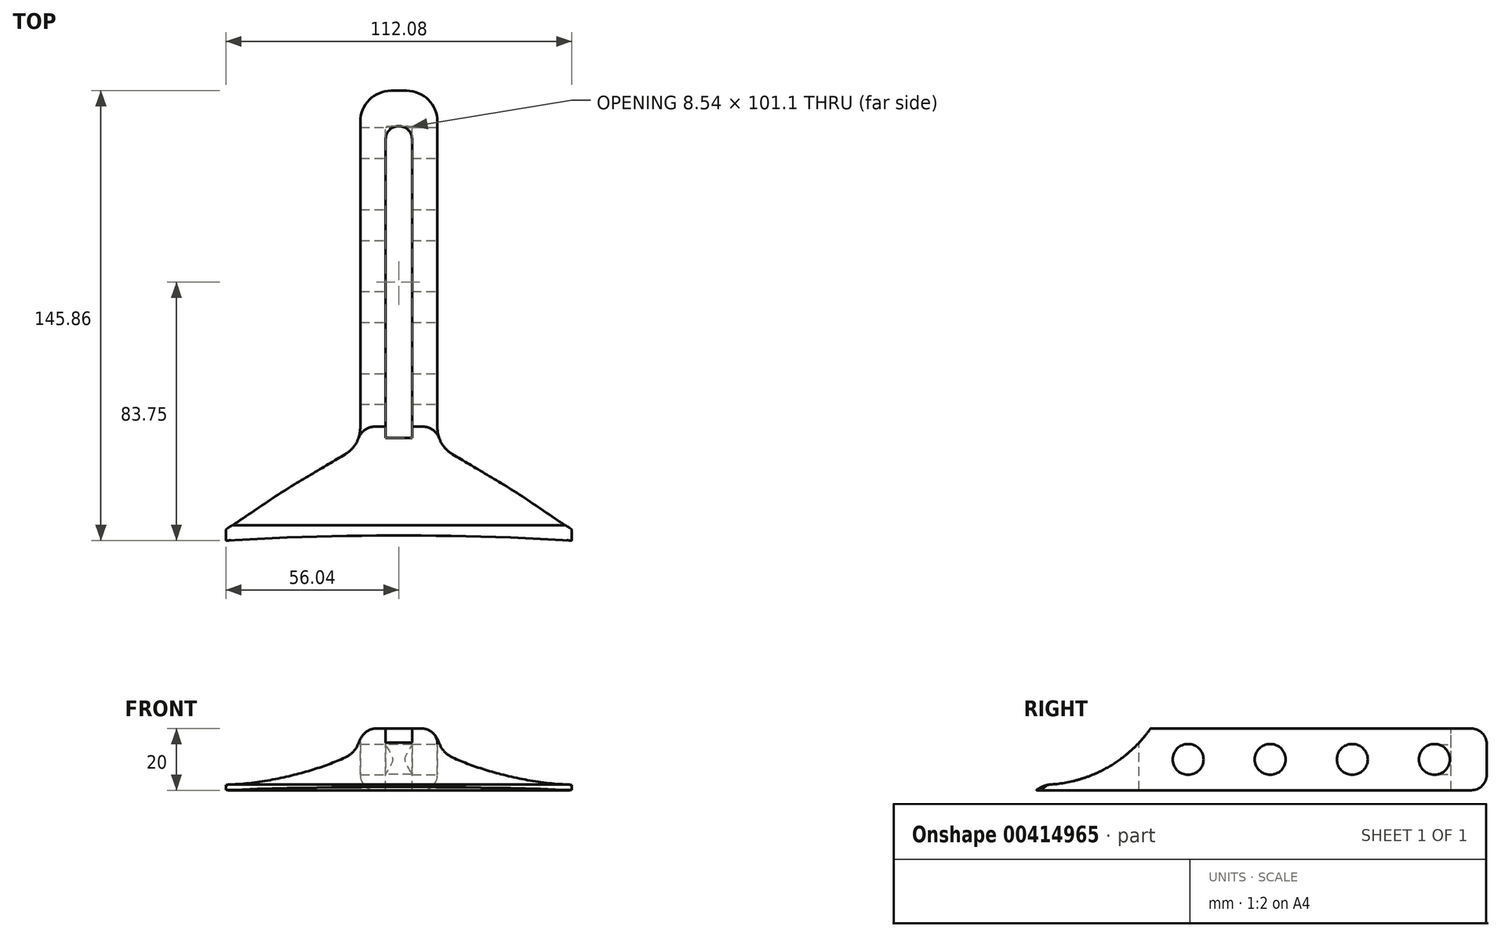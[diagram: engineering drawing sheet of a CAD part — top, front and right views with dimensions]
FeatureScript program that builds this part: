
annotation { "Feature Type Name" : "Feature", "Feature Type Description" : "" }
export const myFeature = defineFeature(function(context is Context, id is Id, definition is map)
    precondition{}
    {
        {
            var Q0;
            Q0=qCreatedBy(makeId("Top.planeOp"),FACE);
            var sketch = newSketch(context, id + "F0", { "sketchPlane" : qUnion([Q0])});
            skLineSegment(sketch, "E0", {"start": v(-12.5, 52.1) * mm, "end": v(-12.5, -52.9) * mm});
            skLineSegment(sketch, "E1", {"start": v(-12.5, -52.9) * mm, "end": v(-56.04, -78.77) * mm});
            skLineSegment(sketch, "E2", {"start": v(-56.04, -78.77) * mm, "end": v(-56.04, -83.77) * mm});
            skLineSegment(sketch, "E3.MirrorCS", {"start": v(12.5, 52.1) * mm, "end": v(12.5, -52.9) * mm});
            skLineSegment(sketch, "E4.MirrorCS", {"start": v(12.5, -52.9) * mm, "end": v(56.04, -78.77) * mm});
            skLineSegment(sketch, "E5.MirrorCS", {"start": v(56.04, -78.77) * mm, "end": v(56.04, -83.77) * mm});
            skLineSegment(sketch, "E6", {"start": v(-2.5, 62.1) * mm, "end": v(2.5, 62.1) * mm});
            skPoint(sketch, "E7.visualSharp", {"position": v(-12.5, 62.1) * mm});
            skArc(sketch, "E7.filletArc", {"start": v(-2.5, 62.1) * mm, "mid": v(-9.57, 59.18) * mm, "end": v(-12.5, 52.1) * mm});
            skPoint(sketch, "E8.visualSharp", {"position": v(12.5, 62.1) * mm});
            skArc(sketch, "E8.filletArc", {"start": v(12.5, 52.1) * mm, "mid": v(9.57, 59.18) * mm, "end": v(2.5, 62.1) * mm});
            skArc(sketch, "E9", {"start": v(56.04, -83.77) * mm, "mid": v(0, -82.13) * mm, "end": v(-56.04, -83.77) * mm});
            skSolve(sketch);
        }
        {
            var Q0;
            Q0=makeQuery(id+"F0.imprint","IMPRINT",FACE,{"disambiguationData":[TD([[makeQuery(id+"F0.imprint","IMPRINT",EDGE,{"derivedFrom":sQuery(id+"F0.wireOp",EDGE,"E0")}),1.0]])]});
            extrude(context, id + "F1", {"entities" : qUnion([Q0]), "depth" : 20 * mm});
        }
        {
            var Q0;
            Q0=makeQuery(id+"F1.opExtrude","SWEPT_EDGE",EDGE,{"disambiguationData":[OSD([sQuery(id+"F0.wireOp",EDGE,"E3.MirrorCS"),sQuery(id+"F0.wireOp",EDGE,"E4.MirrorCS")])]});
            fillet(context, id + "F2", {"entities" : qUnion([Q0]), "radius" : 10 * mm, "tangentPropagation" : true, "allowEdgeOverflow" : false});
        }
        {
            var Q0;
            Q0=makeQuery(id+"F1.opExtrude","SWEPT_EDGE",EDGE,{"disambiguationData":[OSD([sQuery(id+"F0.wireOp",EDGE,"E0"),sQuery(id+"F0.wireOp",EDGE,"E1")])]});
            fillet(context, id + "F3", {"entities" : qUnion([Q0]), "radius" : 10 * mm, "tangentPropagation" : true, "allowEdgeOverflow" : false});
        }
        {
            var Q0;
            Q0=makeQuery(id+"F1.opExtrude","SWEPT_FACE",FACE,{"disambiguationData":[OSD([sQuery(id+"F0.wireOp",EDGE,"E5.MirrorCS")])]});
            var sketch = newSketch(context, id + "F4", { "sketchPlane" : qUnion([Q0])});
            skLineSegment(sketch, "E10", {"start": v(-46.8, 20) * mm, "end": v(-78.77, 20) * mm});
            skLineSegment(sketch, "E11", {"start": v(-78.77, 20) * mm, "end": v(-78.77, 1.88) * mm});
            skArc(sketch, "E12", {"start": v(-78.77, 1.88) * mm, "mid": v(-60.76, 7.35) * mm, "end": v(-46.8, 20) * mm});
            skArc(sketch, "E13", {"start": v(-78.77, 1.88) * mm, "mid": v(-81.43, 1.35) * mm, "end": v(-83.77, 0) * mm});
            skSolve(sketch);
        }
        {
            var Q0;
            Q0=makeQuery(id+"F4.imprint","IMPRINT",FACE,{"disambiguationData":[TD([[makeQuery(id+"F4.imprint","IMPRINT",EDGE,{"derivedFrom":sQuery(id+"F4.wireOp",EDGE,"E11")}),-1.0]])]});
            var Q1;
            Q1=makeQuery(id+"F4.imprint","IMPRINT",FACE,{"disambiguationData":[TD([[makeQuery(id+"F4.imprint","IMPRINT",EDGE,{"derivedFrom":sQuery(id+"F4.wireOp",EDGE,"E10")}),1.0]])]});
            extrude(context, id + "F5", {"entities" : qUnion([Q0, Q1]), "operationType" : NewBodyOperationType.REMOVE, "oppositeDirection" : true, "depth" : 133.5 * mm});
        }
        {
            var Q0;
            Q0=makeQuery(id+"F1.opExtrude","CAP_EDGE",EDGE,{"disambiguationData":[OSD([sQuery(id+"F0.wireOp",EDGE,"E3.MirrorCS")])],"isStart":false});
            var Q1;
            Q1=makeQuery(id+"F1.opExtrude","CAP_EDGE",EDGE,{"disambiguationData":[OSD([sQuery(id+"F0.wireOp",EDGE,"E0")])],"isStart":false});
            var Q2;
            Q2=makeQuery(id+"F1.opExtrude","CAP_EDGE",EDGE,{"disambiguationData":[OSD([sQuery(id+"F0.wireOp",EDGE,"E3.MirrorCS")])],"isStart":true});
            var Q3;
            Q3=makeQuery(id+"F1.opExtrude","CAP_EDGE",EDGE,{"disambiguationData":[OSD([sQuery(id+"F0.wireOp",EDGE,"E0")])],"isStart":true});
            fillet(context, id + "F6", {"entities" : qUnion([Q0, Q1, Q2, Q3]), "radius" : 5 * mm, "tangentPropagation" : true, "allowEdgeOverflow" : false});
        }
        {
            var Q0;
            Q0=makeQuery(id+"F1.opExtrude","CAP_FACE",FACE,{"disambiguationData":[OSD([sQuery(id+"F0.wireOp",EDGE,"E0"),sQuery(id+"F0.wireOp",EDGE,"E1"),sQuery(id+"F0.wireOp",EDGE,"E2"),sQuery(id+"F0.wireOp",EDGE,"UeRdu93e-aRtv-LTrw-fM3b-mN8lGL42KFXm"),sQuery(id+"F0.wireOp",EDGE,"E3.MirrorCS"),sQuery(id+"F0.wireOp",EDGE,"E4.MirrorCS"),sQuery(id+"F0.wireOp",EDGE,"affaa436-bfd7-48af-8192-04fe1cd293190.MirrorCS"),sQuery(id+"F0.wireOp",EDGE,"E5.MirrorCS"),sQuery(id+"F0.wireOp",EDGE,"E6"),sQuery(id+"F0.wireOp",EDGE,"E7.filletArc"),sQuery(id+"F0.wireOp",EDGE,"E8.filletArc")])],"isStart":false});
            var sketch = newSketch(context, id + "F7", { "sketchPlane" : qUnion([Q0])});
            skLineSegment(sketch, "E14.bottom", {"start": v(-4.27, 50.55) * mm, "end": v(4.27, 50.55) * mm});
            skLineSegment(sketch, "E14.top", {"start": v(-4.27, -50.55) * mm, "end": v(4.27, -50.55) * mm});
            skLineSegment(sketch, "E14.left", {"start": v(-4.27, 50.55) * mm, "end": v(-4.27, -50.55) * mm});
            skLineSegment(sketch, "E14.right", {"start": v(4.27, 50.55) * mm, "end": v(4.27, -50.55) * mm});
            skPoint(sketch, "E14.middle", {"position": v(0, 0) * mm});
            skSolve(sketch);
        }
        {
            var Q0;
            {var subQ0=sQuery(id+"F7.wireOp",EDGE,"E14.bottom");Q0=makeQuery(id+"F7.imprint","IMPRINT",FACE,{"disambiguationData":[TD([[makeQuery(id+"F7.imprint","IMPRINT",EDGE,{"derivedFrom":subQ0}),-1.0]])]});}
            var Q1;
            {var subQ0=sQuery(id+"F7.wireOp",EDGE,"E14.top");Q1=makeQuery(id+"F7.imprint","IMPRINT",FACE,{"disambiguationData":[TD([[makeQuery(id+"F7.imprint","IMPRINT",EDGE,{"derivedFrom":subQ0}),1.0]])]});}
            extrude(context, id + "F8", {"entities" : qUnion([Q0, Q1]), "operationType" : NewBodyOperationType.REMOVE, "oppositeDirection" : true, "depth" : 46 * mm});
        }
        {
            var Q0;
            Q0=makeQuery(id+"F8.boolean.opBoolean","COPY",EDGE,{"derivedFrom":makeQuery(id+"F8.opExtrude","SWEPT_EDGE",EDGE,{"disambiguationData":[OSD([sQuery(id+"F7.wireOp",EDGE,"E14.bottom"),sQuery(id+"F7.wireOp",EDGE,"E14.left")])]})});
            var Q1;
            Q1=makeQuery(id+"F8.boolean.opBoolean","COPY",EDGE,{"derivedFrom":makeQuery(id+"F8.opExtrude","SWEPT_EDGE",EDGE,{"disambiguationData":[OSD([sQuery(id+"F7.wireOp",EDGE,"E14.bottom"),sQuery(id+"F7.wireOp",EDGE,"E14.right")])]})});
            fillet(context, id + "F9", {"entities" : qUnion([Q0, Q1]), "radius" : 4 * mm, "tangentPropagation" : true, "allowEdgeOverflow" : false});
        }
        {
            var Q0;
            Q0=makeQuery(id+"F1.opExtrude","SWEPT_FACE",FACE,{"disambiguationData":[OSD([sQuery(id+"F0.wireOp",EDGE,"E3.MirrorCS")])]});
            var sketch = newSketch(context, id + "F10", { "sketchPlane" : qUnion([Q0])});
            skCircle(sketch, "E15", {"center": v(45.17, 10) * mm, "radius": 5 * mm});
            skPoint(sketch, "E15.centerSnap0", {"position": v(52.1, 10) * mm});
            skCircle(sketch, "E16.1.0.0", {"center": v(18.57, 10) * mm, "radius": 5 * mm});
            skCircle(sketch, "E16.2.0.0", {"center": v(-8.03, 10) * mm, "radius": 5 * mm});
            skCircle(sketch, "E16.3.0.0", {"center": v(-34.63, 10) * mm, "radius": 5 * mm});
            skLineSegment(sketch, "E16.direction1", {"start": v(45.17, 10) * mm, "end": v(18.57, 10) * mm, "construction": true});
            skSolve(sketch);
        }
        {
            var Q0;
            {var subQ0=sQuery(id+"F10.wireOp",EDGE,"E16.3.0.0");var subQ1=sQuery(id+"F0.wireOp",EDGE,"E3.MirrorCS");var subQ2=makeQuery(id+"F1.opExtrude","SWEPT_FACE",FACE,{"disambiguationData":[OSD([subQ1])]});var subQ3=makeQuery(id+"F10.imprint","INTERSECT",VERTEX,{"derivedFrom":[makeQuery(id+"F6.opFillet","BLEND_EDGE",EDGE,{"blendedFrom":[makeQuery(id+"F1.opExtrude","CAP_EDGE",EDGE,{"disambiguationData":[OSD([subQ1])],"isStart":true}),subQ2],"blendedInto":[subQ2]}),subQ0]});Q0=makeQuery(id+"F10.imprint","IMPRINT",FACE,{"disambiguationData":[TD([[makeQuery(id+"F10.imprint","IMPRINT",EDGE,{"disambiguationData":[TD([[subQ3,1.0]])],"derivedFrom":subQ0}),1.0]])]});}
            var Q1;
            {var subQ0=sQuery(id+"F10.wireOp",EDGE,"E16.2.0.0");var subQ1=sQuery(id+"F0.wireOp",EDGE,"E3.MirrorCS");var subQ2=makeQuery(id+"F1.opExtrude","SWEPT_FACE",FACE,{"disambiguationData":[OSD([subQ1])]});var subQ3=makeQuery(id+"F10.imprint","INTERSECT",VERTEX,{"derivedFrom":[makeQuery(id+"F6.opFillet","BLEND_EDGE",EDGE,{"blendedFrom":[makeQuery(id+"F1.opExtrude","CAP_EDGE",EDGE,{"disambiguationData":[OSD([subQ1])],"isStart":true}),subQ2],"blendedInto":[subQ2]}),subQ0]});Q1=makeQuery(id+"F10.imprint","IMPRINT",FACE,{"disambiguationData":[TD([[makeQuery(id+"F10.imprint","IMPRINT",EDGE,{"disambiguationData":[TD([[subQ3,1.0]])],"derivedFrom":subQ0}),1.0]])]});}
            var Q2;
            {var subQ0=sQuery(id+"F10.wireOp",EDGE,"E16.1.0.0");var subQ1=sQuery(id+"F0.wireOp",EDGE,"E3.MirrorCS");var subQ2=makeQuery(id+"F1.opExtrude","SWEPT_FACE",FACE,{"disambiguationData":[OSD([subQ1])]});var subQ3=makeQuery(id+"F10.imprint","INTERSECT",VERTEX,{"derivedFrom":[makeQuery(id+"F6.opFillet","BLEND_EDGE",EDGE,{"blendedFrom":[makeQuery(id+"F1.opExtrude","CAP_EDGE",EDGE,{"disambiguationData":[OSD([subQ1])],"isStart":true}),subQ2],"blendedInto":[subQ2]}),subQ0]});Q2=makeQuery(id+"F10.imprint","IMPRINT",FACE,{"disambiguationData":[TD([[makeQuery(id+"F10.imprint","IMPRINT",EDGE,{"disambiguationData":[TD([[subQ3,1.0]])],"derivedFrom":subQ0}),1.0]])]});}
            var Q3;
            {var subQ0=sQuery(id+"F10.wireOp",EDGE,"E15");var subQ1=sQuery(id+"F0.wireOp",EDGE,"E3.MirrorCS");var subQ2=makeQuery(id+"F1.opExtrude","SWEPT_FACE",FACE,{"disambiguationData":[OSD([subQ1])]});var subQ3=makeQuery(id+"F10.imprint","INTERSECT",VERTEX,{"derivedFrom":[makeQuery(id+"F6.opFillet","BLEND_EDGE",EDGE,{"blendedFrom":[makeQuery(id+"F1.opExtrude","CAP_EDGE",EDGE,{"disambiguationData":[OSD([subQ1])],"isStart":true}),subQ2],"blendedInto":[subQ2]}),subQ0]});Q3=makeQuery(id+"F10.imprint","IMPRINT",FACE,{"disambiguationData":[TD([[makeQuery(id+"F10.imprint","IMPRINT",EDGE,{"disambiguationData":[TD([[subQ3,1.0]])],"derivedFrom":subQ0}),1.0]])]});}
            extrude(context, id + "F11", {"entities" : qUnion([Q0, Q1, Q2, Q3]), "operationType" : NewBodyOperationType.REMOVE, "oppositeDirection" : true, "depth" : 42.1 * mm});
        }
    });
